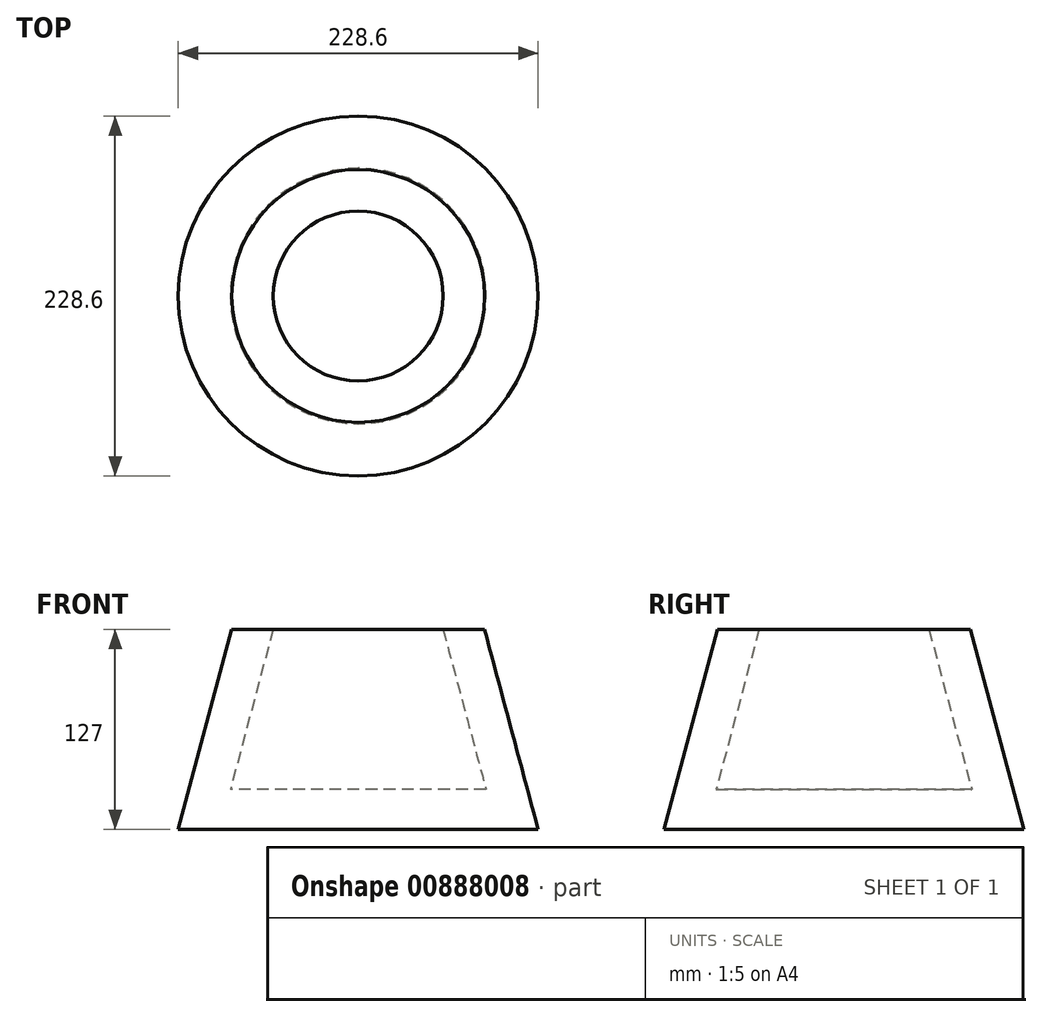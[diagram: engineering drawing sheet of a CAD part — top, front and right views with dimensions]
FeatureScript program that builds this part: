
annotation { "Feature Type Name" : "Feature", "Feature Type Description" : "" }
export const myFeature = defineFeature(function(context is Context, id is Id, definition is map)
    precondition{}
    {
        {
            var Q0;
            Q0=qCreatedBy(makeId("Top.planeOp"),FACE);
            var sketch = newSketch(context, id + "F0", { "sketchPlane" : qUnion([Q0])});
            skCircle(sketch, "E0", {"center": v(0, 0) * mm, "radius": 114.3 * mm});
            skSolve(sketch);
        }
        {
            var Q0;
            Q0=makeQuery(id+"F0.imprint","IMPRINT",FACE,{"disambiguationData":[TD([[makeQuery(id+"F0.imprint","IMPRINT",EDGE,{"derivedFrom":sQuery(id+"F0.wireOp",EDGE,"E0")}),1.0]])]});
            extrude(context, id + "F1", {"entities" : qUnion([Q0]), "depth" : 127 * mm, "offsetDistance" : 25.4 * mm, "hasDraft" : true, "draftAngle" : 15 * degree, "draftPullDirection" : true});
        }
        {
            var Q0;
            Q0=makeQuery(id+"F1.opExtrude","CAP_FACE",FACE,{"disambiguationData":[OSD([sQuery(id+"F0.wireOp",EDGE,"E0")])],"isStart":false});
            shell(context, id + "F2", {"entities" : qUnion([Q0]), "thickness" : 25.4 * mm});
        }
    });
